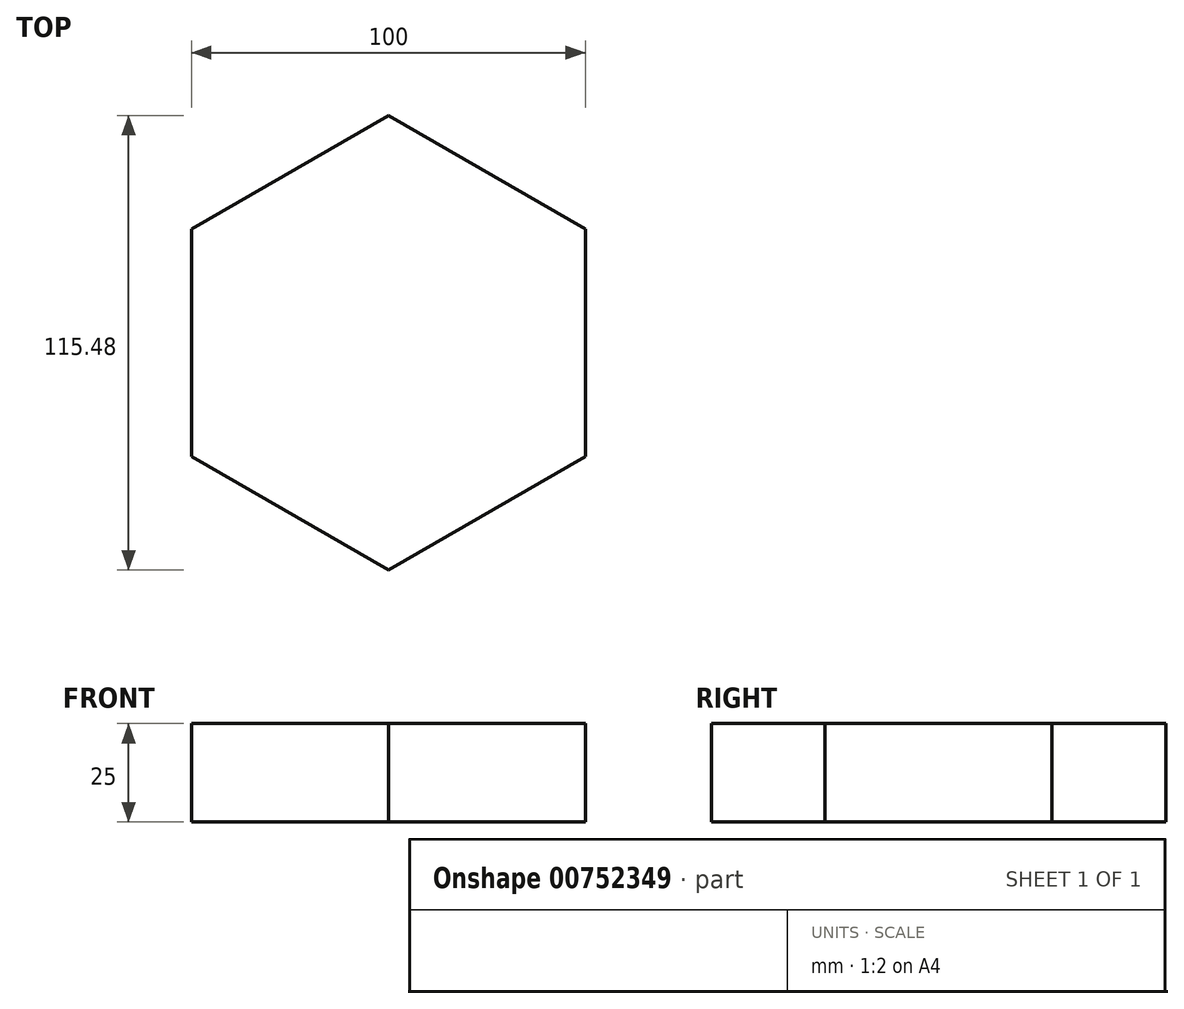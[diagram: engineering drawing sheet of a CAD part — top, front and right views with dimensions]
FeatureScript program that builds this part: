
annotation { "Feature Type Name" : "Feature", "Feature Type Description" : "" }
export const myFeature = defineFeature(function(context is Context, id is Id, definition is map)
    precondition{}
    {
        {
            var Q0;
            Q0=qCreatedBy(makeId("Top.planeOp"),FACE);
            var sketch = newSketch(context, id + "F0", { "sketchPlane" : qUnion([Q0])});
            skCircle(sketch, "E0.cCircle", {"center": v(0, 0) * mm, "radius": 50 * mm, "construction": true});
            skLineSegment(sketch, "E0.0", {"start": v(-50, 28.87) * mm, "end": v(0, 57.74) * mm});
            skLineSegment(sketch, "E0.1", {"start": v(0, 57.74) * mm, "end": v(50, 28.87) * mm});
            skLineSegment(sketch, "E0.2", {"start": v(50, 28.87) * mm, "end": v(50, -28.87) * mm});
            skLineSegment(sketch, "E0.3", {"start": v(50, -28.87) * mm, "end": v(0, -57.74) * mm});
            skLineSegment(sketch, "E0.4", {"start": v(0, -57.74) * mm, "end": v(-50, -28.87) * mm});
            skLineSegment(sketch, "E0.5", {"start": v(-50, -28.87) * mm, "end": v(-50, 28.87) * mm});
            skPoint(sketch, "E0.0.midPoint", {"position": v(-25, 43.3) * mm});
            skSolve(sketch);
        }
        {
            var Q0;
            Q0=makeQuery(id+"F0.imprint","IMPRINT",FACE,{"disambiguationData":[TD([[makeQuery(id+"F0.imprint","IMPRINT",EDGE,{"derivedFrom":sQuery(id+"F0.wireOp",EDGE,"E0.0")}),-1.0]])]});
            extrude(context, id + "F1", {"entities" : qUnion([Q0]), "depth" : 25 * mm, "offsetDistance" : 25 * mm});
        }
        {
            var Q0;
            Q0=makeQuery(id+"F1.opExtrude","CAP_FACE",FACE,{"disambiguationData":[OSD([sQuery(id+"F0.wireOp",EDGE,"E0.0"),sQuery(id+"F0.wireOp",EDGE,"E0.1"),sQuery(id+"F0.wireOp",EDGE,"E0.2"),sQuery(id+"F0.wireOp",EDGE,"E0.3"),sQuery(id+"F0.wireOp",EDGE,"E0.4"),sQuery(id+"F0.wireOp",EDGE,"E0.5")])],"isStart":true});
            cPlane(context, id + "F2", {"entities" : qUnion([Q0]), "cplaneType" : CPlaneType.OFFSET, "offset" : 50 * mm, "width" : 150 * mm, "height" : 150 * mm});
        }
    });
